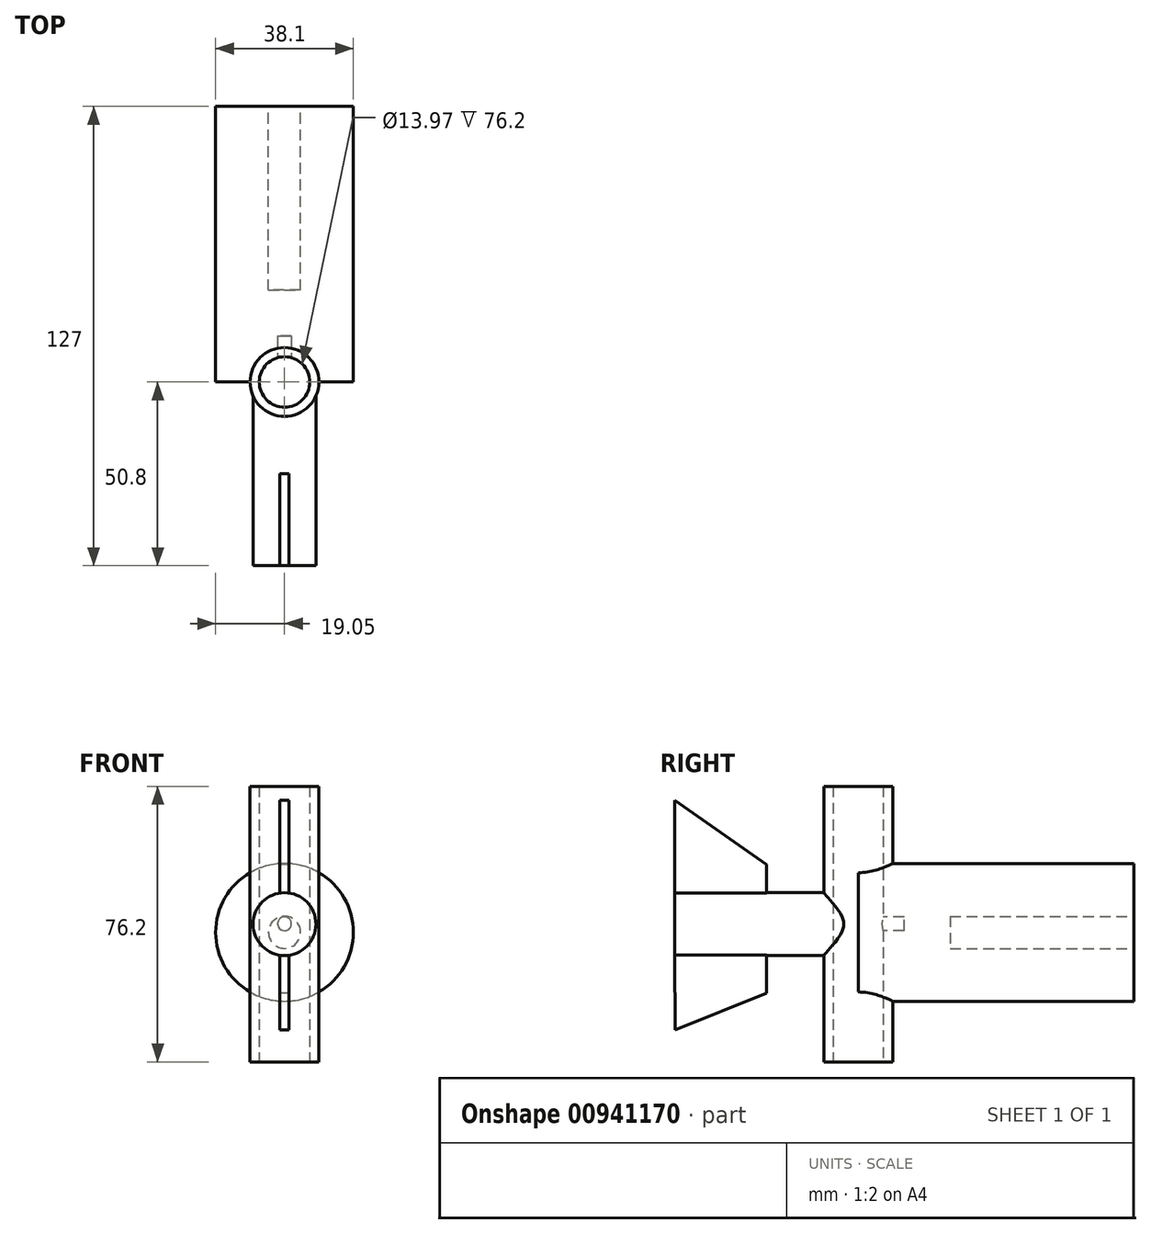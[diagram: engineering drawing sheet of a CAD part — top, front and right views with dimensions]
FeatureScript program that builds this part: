
annotation { "Feature Type Name" : "Feature", "Feature Type Description" : "" }
export const myFeature = defineFeature(function(context is Context, id is Id, definition is map)
    precondition{}
    {
        {
            var Q0;
            Q0=qCreatedBy(makeId("Top.planeOp"),FACE);
            var sketch = newSketch(context, id + "F0", { "sketchPlane" : qUnion([Q0])});
            skCircle(sketch, "E0", {"center": v(0, 0) * mm, "radius": 6.99 * mm});
            skCircle(sketch, "E1", {"center": v(0, 0) * mm, "radius": 9.53 * mm});
            skSolve(sketch);
        }
        {
            var Q0;
            Q0=makeQuery(id+"F0.imprint","IMPRINT",FACE,{"disambiguationData":[TD([[makeQuery(id+"F0.imprint","IMPRINT",EDGE,{"derivedFrom":sQuery(id+"F0.wireOp",EDGE,"E0")}),-1.0]])]});
            extrude(context, id + "F1", {"entities" : qUnion([Q0]), "depth" : 76.2 * mm, "offsetDistance" : 25.4 * mm});
        }
        {
            var Q0;
            Q0=qCreatedBy(makeId("Front.planeOp"),FACE);
            var sketch = newSketch(context, id + "F2", { "sketchPlane" : qUnion([Q0])});
            skCircle(sketch, "E2", {"center": v(0, 38.1) * mm, "radius": 8.7 * mm});
            skSolve(sketch);
        }
        {
            var Q0;
            Q0 = qSketchRegion(id + "F2", true);
            extrude(context, id + "F3", {"entities" : qUnion([Q0]), "operationType" : NewBodyOperationType.ADD, "depth" : 50.8 * mm, "offsetDistance" : 25.4 * mm});
        }
        {
            var Q0;
            Q0=qCreatedBy(makeId("Right.planeOp"),FACE);
            var sketch = newSketch(context, id + "F4", { "sketchPlane" : qUnion([Q0])});
            skLineSegment(sketch, "E3", {"start": v(-50.8, 47) * mm, "end": v(-50.8, 72.4) * mm});
            skLineSegment(sketch, "E4", {"start": v(-50.8, 72.4) * mm, "end": v(-25.4, 54.6) * mm});
            skLineSegment(sketch, "E5", {"start": v(-25.4, 54.61) * mm, "end": v(-25.4, 47) * mm});
            skLineSegment(sketch, "E6", {"start": v(-25.4, 47) * mm, "end": v(-50.8, 47) * mm});
            skLineSegment(sketch, "E7", {"start": v(-25.4, 47) * mm, "end": v(-25.4, 19.05) * mm});
            skLineSegment(sketch, "E8", {"start": v(-25.4, 19.05) * mm, "end": v(-50.65, 8.9) * mm});
            skLineSegment(sketch, "E9", {"start": v(-50.65, 8.9) * mm, "end": v(-50.8, 47) * mm});
            skSolve(sketch);
        }
        {
            var Q0;
            Q0 = qSketchRegion(id + "F4", true);
            extrude(context, id + "F5", {"entities" : qUnion([Q0]), "operationType" : NewBodyOperationType.ADD, "depth" : 1.27 * mm, "offsetDistance" : 25.4 * mm, "hasSecondDirection" : true, "secondDirectionOppositeDirection" : true, "secondDirectionDepth" : 1.27 * mm});
        }
        {
            var Q0;
            Q0=qCreatedBy(makeId("Top.planeOp"),FACE);
            var sketch = newSketch(context, id + "F6", { "sketchPlane" : qUnion([Q0])});
            skCircle(sketch, "E10", {"center": v(0, 0) * mm, "radius": 6.99 * mm});
            skSolve(sketch);
        }
        {
            var Q0;
            Q0 = qSketchRegion(id + "F6", true);
            extrude(context, id + "F7", {"entities" : qUnion([Q0]), "operationType" : NewBodyOperationType.REMOVE, "depth" : 76.2 * mm, "offsetDistance" : 25.4 * mm});
        }
        {
            var Q0;
            Q0=qCreatedBy(makeId("Right.planeOp"),FACE);
            var sketch = newSketch(context, id + "F8", { "sketchPlane" : qUnion([Q0])});
            skLineSegment(sketch, "E11.bottom", {"start": v(0, 54.87) * mm, "end": v(76.2, 54.87) * mm});
            skLineSegment(sketch, "E11.top", {"start": v(0, 16.77) * mm, "end": v(76.2, 16.77) * mm});
            skLineSegment(sketch, "E11.left", {"start": v(0, 54.87) * mm, "end": v(0, 16.77) * mm});
            skLineSegment(sketch, "E11.right", {"start": v(76.2, 54.87) * mm, "end": v(76.2, 16.77) * mm});
            skLineSegment(sketch, "E12", {"start": v(0, 35.82) * mm, "end": v(89.32, 35.82) * mm});
            skSolve(sketch);
        }
        {
            var Q0;
            {var subQ0=sQuery(id+"F8.wireOp",EDGE,"E11.bottom");Q0=makeQuery(id+"F8.imprint","IMPRINT",FACE,{"disambiguationData":[TD([[makeQuery(id+"F8.imprint","IMPRINT",EDGE,{"derivedFrom":subQ0}),-1.0]])]});}
            var Q1;
            Q1=sQuery(id+"F8.wireOp",EDGE,"E12");
            revolve(context, id + "F9", {"operationType" : NewBodyOperationType.ADD, "surfaceOperationType" : NewSurfaceOperationType.NEW, "entities" : qUnion([Q0]), "axis" : qUnion([Q1]), "revolveType" : RevolveType.FULL});
        }
        {
            var Q0;
            Q0=makeQuery(id+"F9.opRevolve","SWEPT_FACE",FACE,{"disambiguationData":[OSD([sQuery(id+"F8.wireOp",EDGE,"E11.right")])]});
            var sketch = newSketch(context, id + "F10", { "sketchPlane" : qUnion([Q0])});
            skCircle(sketch, "E13", {"center": v(0, 35.82) * mm, "radius": 4.45 * mm});
            skSolve(sketch);
        }
        {
            var Q0;
            Q0=makeQuery(id+"F10.imprint","IMPRINT",FACE,{"disambiguationData":[TD([[makeQuery(id+"F10.imprint","IMPRINT",EDGE,{"derivedFrom":sQuery(id+"F10.wireOp",EDGE,"E13")}),1.0]])]});
            extrude(context, id + "F11", {"entities" : qUnion([Q0]), "operationType" : NewBodyOperationType.REMOVE, "oppositeDirection" : true, "depth" : 50.8 * mm, "offsetDistance" : 25.4 * mm});
        }
        {
            var Q0;
            Q0 = qSketchRegion(id + "F6", true);
            extrude(context, id + "F12", {"entities" : qUnion([Q0]), "operationType" : NewBodyOperationType.REMOVE, "depth" : 87.88 * mm, "offsetDistance" : 25.4 * mm});
        }
        {
            var Q0;
            Q0=qCreatedBy(makeId("Front.planeOp"),FACE);
            var sketch = newSketch(context, id + "F13", { "sketchPlane" : qUnion([Q0])});
            skCircle(sketch, "E14", {"center": v(0, 38.18) * mm, "radius": 1.9 * mm});
            skSolve(sketch);
        }
        {
            var Q0;
            Q0 = qSketchRegion(id + "F13", true);
            extrude(context, id + "F14", {"entities" : qUnion([Q0]), "operationType" : NewBodyOperationType.REMOVE, "oppositeDirection" : true, "depth" : 12.7 * mm, "offsetDistance" : 25.4 * mm});
        }
    });
